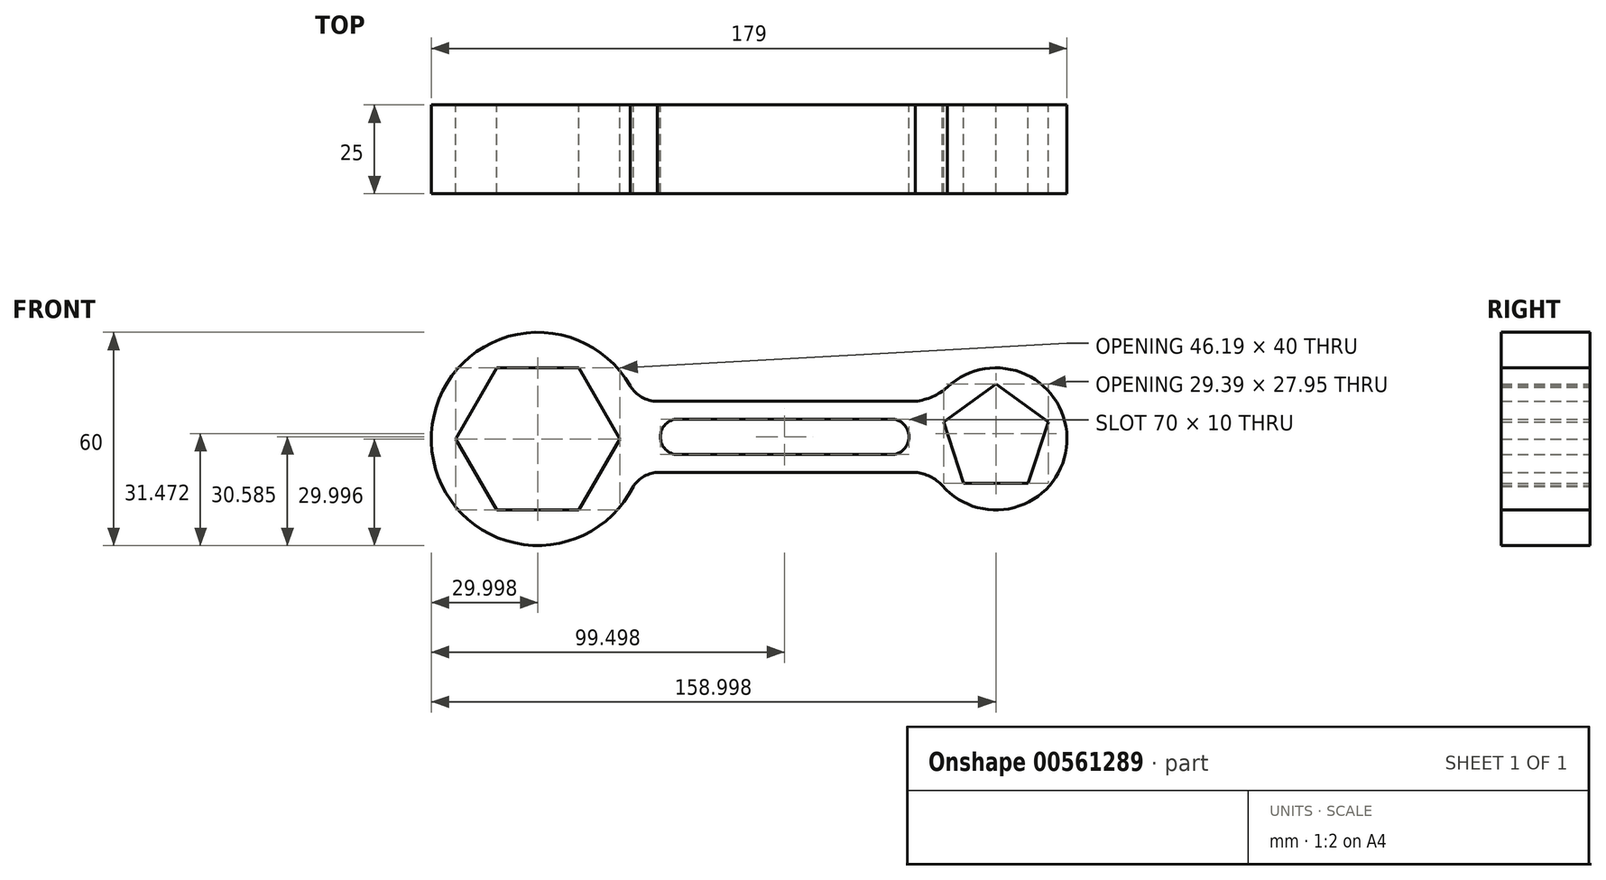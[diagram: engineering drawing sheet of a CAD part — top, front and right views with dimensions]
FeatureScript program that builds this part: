
annotation { "Feature Type Name" : "Feature", "Feature Type Description" : "" }
export const myFeature = defineFeature(function(context is Context, id is Id, definition is map)
    precondition{}
    {
        {
            var Q0;
            Q0=qCreatedBy(makeId("Front.planeOp"),FACE);
            var sketch = newSketch(context, id + "F0", { "sketchPlane" : qUnion([Q0])});
            skCircle(sketch, "E0", {"center": v(-74.06, 18.86) * mm, "radius": 30 * mm});
            skCircle(sketch, "E1", {"center": v(54.94, 18.86) * mm, "radius": 20 * mm});
            skLineSegment(sketch, "E2.0", {"start": v(-62.51, -1.14) * mm, "end": v(-85.6, -1.14) * mm});
            skLineSegment(sketch, "E2.1", {"start": v(-85.6, -1.14) * mm, "end": v(-97.16, 18.86) * mm});
            skLineSegment(sketch, "E2.2", {"start": v(-97.16, 18.86) * mm, "end": v(-85.6, 38.86) * mm});
            skLineSegment(sketch, "E2.3", {"start": v(-85.6, 38.86) * mm, "end": v(-62.51, 38.86) * mm});
            skLineSegment(sketch, "E2.4", {"start": v(-62.51, 38.86) * mm, "end": v(-50.97, 18.86) * mm});
            skLineSegment(sketch, "E2.5", {"start": v(-50.97, 18.86) * mm, "end": v(-62.51, -1.14) * mm});
            skPoint(sketch, "E2.0.midPoint", {"position": v(-74.06, -1.14) * mm});
            skLineSegment(sketch, "E3.0", {"start": v(64.02, 6.36) * mm, "end": v(45.86, 6.36) * mm});
            skLineSegment(sketch, "E3.1", {"start": v(45.86, 6.36) * mm, "end": v(40.24, 23.63) * mm});
            skLineSegment(sketch, "E3.2", {"start": v(40.24, 23.63) * mm, "end": v(54.94, 34.3) * mm});
            skLineSegment(sketch, "E3.3", {"start": v(54.94, 34.3) * mm, "end": v(69.63, 23.63) * mm});
            skLineSegment(sketch, "E3.4", {"start": v(69.63, 23.63) * mm, "end": v(64.02, 6.36) * mm});
            skPoint(sketch, "E3.0.midPoint", {"position": v(54.94, 6.36) * mm});
            skPoint(sketch, "E4.startSnap0", {"position": v(-74.06, 38.86) * mm});
            skPoint(sketch, "E4.endSnap0", {"position": v(-74.06, 38.86) * mm});
            skLineSegment(sketch, "E5", {"start": v(-39.94, 9.45) * mm, "end": v(32.27, 9.45) * mm});
            skLineSegment(sketch, "E6", {"start": v(-40.44, 29.45) * mm, "end": v(32.24, 29.45) * mm});
            skPoint(sketch, "E7.start.orphan", {"position": v(-44.06, 18.86) * mm});
            skLineSegment(sketch, "E8.bottom", {"start": v(-34.56, 14.45) * mm, "end": v(25.44, 14.45) * mm});
            skLineSegment(sketch, "E8.top", {"start": v(-34.56, 24.45) * mm, "end": v(25.44, 24.45) * mm});
            skLineSegment(sketch, "E8.left", {"start": v(-39.56, 19.45) * mm, "end": v(-39.56, 19.45) * mm});
            skLineSegment(sketch, "E8.right", {"start": v(30.44, 19.45) * mm, "end": v(30.44, 19.45) * mm});
            skPoint(sketch, "E9.visualSharp", {"position": v(30.44, 24.45) * mm});
            skArc(sketch, "E9.filletArc", {"start": v(30.44, 19.45) * mm, "mid": v(28.97, 22.98) * mm, "end": v(25.44, 24.45) * mm});
            skPoint(sketch, "E10.visualSharp", {"position": v(30.44, 14.45) * mm});
            skArc(sketch, "E10.filletArc", {"start": v(25.44, 14.45) * mm, "mid": v(28.97, 15.9) * mm, "end": v(30.44, 19.45) * mm});
            skPoint(sketch, "E11.visualSharp", {"position": v(-39.56, 14.45) * mm});
            skArc(sketch, "E11.filletArc", {"start": v(-39.56, 19.45) * mm, "mid": v(-38.1, 15.9) * mm, "end": v(-34.56, 14.45) * mm});
            skPoint(sketch, "E12.visualSharp", {"position": v(-39.56, 24.45) * mm});
            skArc(sketch, "E12.filletArc", {"start": v(-34.56, 24.45) * mm, "mid": v(-38.1, 22.98) * mm, "end": v(-39.56, 19.45) * mm});
            skArc(sketch, "E13", {"start": v(-48.08, 33.85) * mm, "mid": v(-44.75, 30.6) * mm, "end": v(-40.24, 29.45) * mm});
            skArc(sketch, "E14", {"start": v(-39.56, 9.45) * mm, "mid": v(-44.68, 7.97) * mm, "end": v(-48.08, 3.86) * mm});
            skArc(sketch, "E15", {"start": v(32.24, 29.45) * mm, "mid": v(37.33, 30.89) * mm, "end": v(41.7, 33.85) * mm});
            skArc(sketch, "E16", {"start": v(40.2, 5.34) * mm, "mid": v(36.63, 8.16) * mm, "end": v(32.27, 9.45) * mm});
            skSolve(sketch);
        }
        {
            var Q0;
            Q0 = qSketchRegion(id + "F0", true);
            extrude(context, id + "F1", {"entities" : qUnion([Q0]), "depth" : 25 * mm, "offsetDistance" : 25 * mm});
        }
    });
